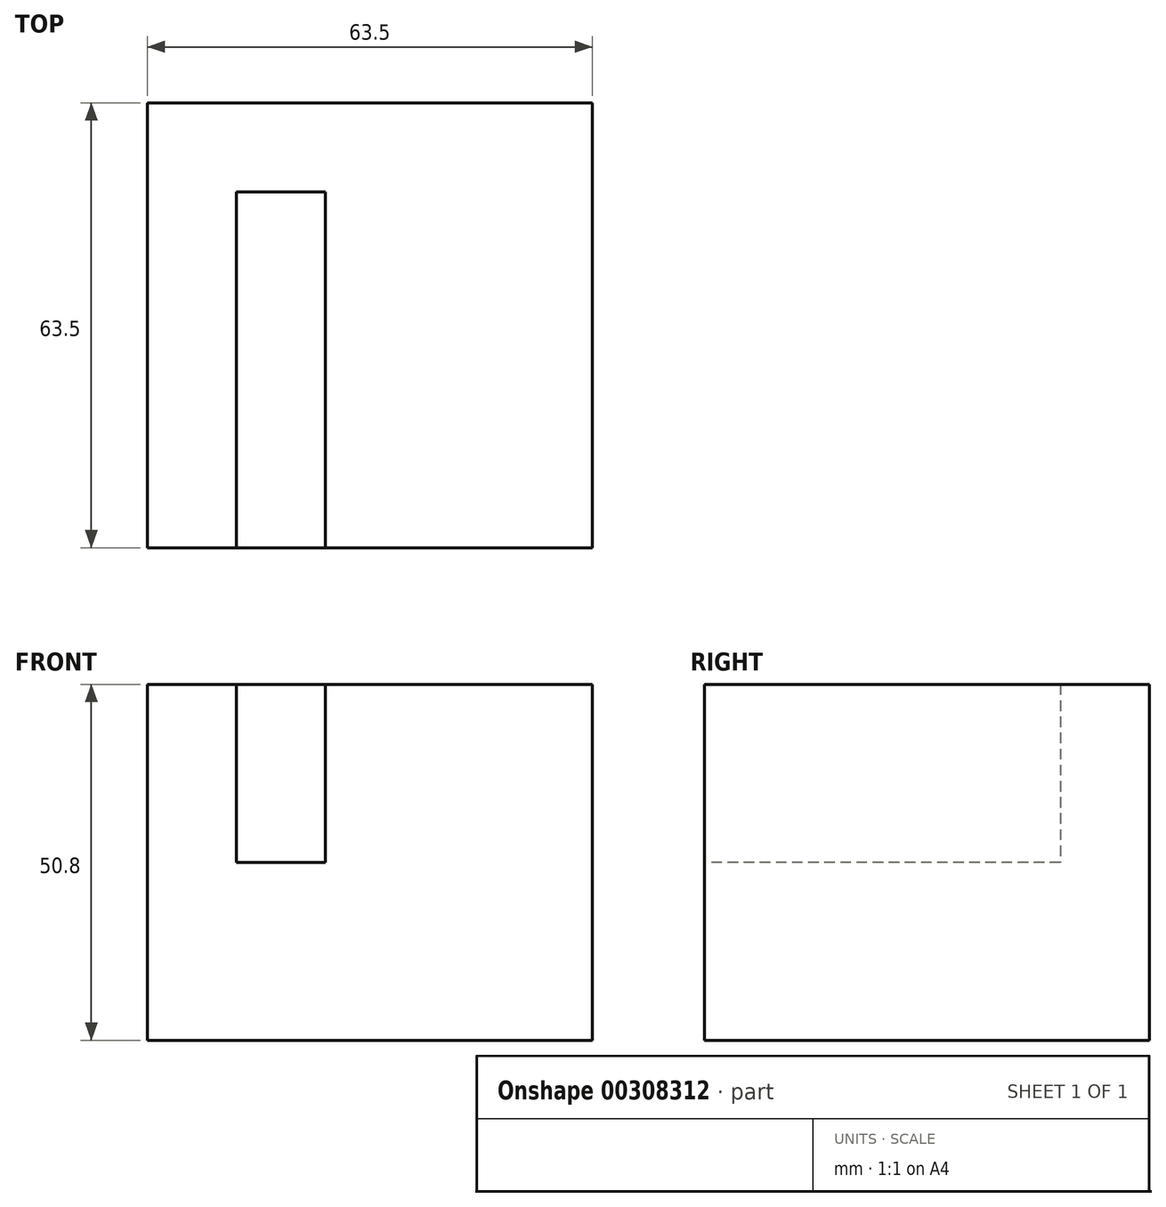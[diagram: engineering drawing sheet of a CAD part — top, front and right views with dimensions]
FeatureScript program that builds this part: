
annotation { "Feature Type Name" : "Feature", "Feature Type Description" : "" }
export const myFeature = defineFeature(function(context is Context, id is Id, definition is map)
    precondition{}
    {
        {
            var Q0;
            Q0=qCreatedBy(makeId("Front.planeOp"),FACE);
            var sketch = newSketch(context, id + "F0", { "sketchPlane" : qUnion([Q0])});
            skLineSegment(sketch, "E0", {"start": v(-28.2, -26.95) * mm, "end": v(35.3, -26.95) * mm});
            skLineSegment(sketch, "E1", {"start": v(-28.2, -26.95) * mm, "end": v(-28.2, 23.85) * mm});
            skLineSegment(sketch, "E2", {"start": v(-28.2, 23.85) * mm, "end": v(35.3, 23.85) * mm});
            skLineSegment(sketch, "E3", {"start": v(35.3, 23.85) * mm, "end": v(35.3, -26.95) * mm});
            skSolve(sketch);
        }
        {
            var Q0;
            Q0=makeQuery(id+"F0.imprint","IMPRINT",FACE,{"disambiguationData":[TD([[makeQuery(id+"F0.imprint","IMPRINT",EDGE,{"derivedFrom":sQuery(id+"F0.wireOp",EDGE,"E0")}),1.0]])]});
            extrude(context, id + "F1", {"entities" : qUnion([Q0]), "depth" : 63.5 * mm});
        }
        {
            var Q0;
            Q0=makeQuery(id+"F1.opExtrude","CAP_FACE",FACE,{"disambiguationData":[OSD([sQuery(id+"F0.wireOp",EDGE,"E0"),sQuery(id+"F0.wireOp",EDGE,"E1"),sQuery(id+"F0.wireOp",EDGE,"E2"),sQuery(id+"F0.wireOp",EDGE,"E3")])],"isStart":false});
            var sketch = newSketch(context, id + "F2", { "sketchPlane" : qUnion([Q0])});
            skLineSegment(sketch, "E4.bottom", {"start": v(-15.5, 23.85) * mm, "end": v(-2.8, 23.85) * mm});
            skLineSegment(sketch, "E4.top", {"start": v(-15.5, -1.55) * mm, "end": v(-2.8, -1.55) * mm});
            skLineSegment(sketch, "E4.left", {"start": v(-15.5, 23.85) * mm, "end": v(-15.5, -1.55) * mm});
            skLineSegment(sketch, "E4.right", {"start": v(-2.8, 23.85) * mm, "end": v(-2.8, -1.55) * mm});
            skLineSegment(sketch, "E5", {"start": v(-28.2, 23.85) * mm, "end": v(-15.5, 23.85) * mm});
            skLineSegment(sketch, "E6", {"start": v(-2.8, 23.85) * mm, "end": v(35.3, 23.85) * mm});
            skSolve(sketch);
        }
        {
            var Q0;
            Q0=makeQuery(id+"F2.imprint","IMPRINT",FACE,{"disambiguationData":[TD([[makeQuery(id+"F2.imprint","IMPRINT",EDGE,{"derivedFrom":sQuery(id+"F2.wireOp",EDGE,"E4.bottom")}),-1.0]])]});
            extrude(context, id + "F3", {"entities" : qUnion([Q0]), "operationType" : NewBodyOperationType.REMOVE, "oppositeDirection" : true, "depth" : 50.8 * mm});
        }
    });
